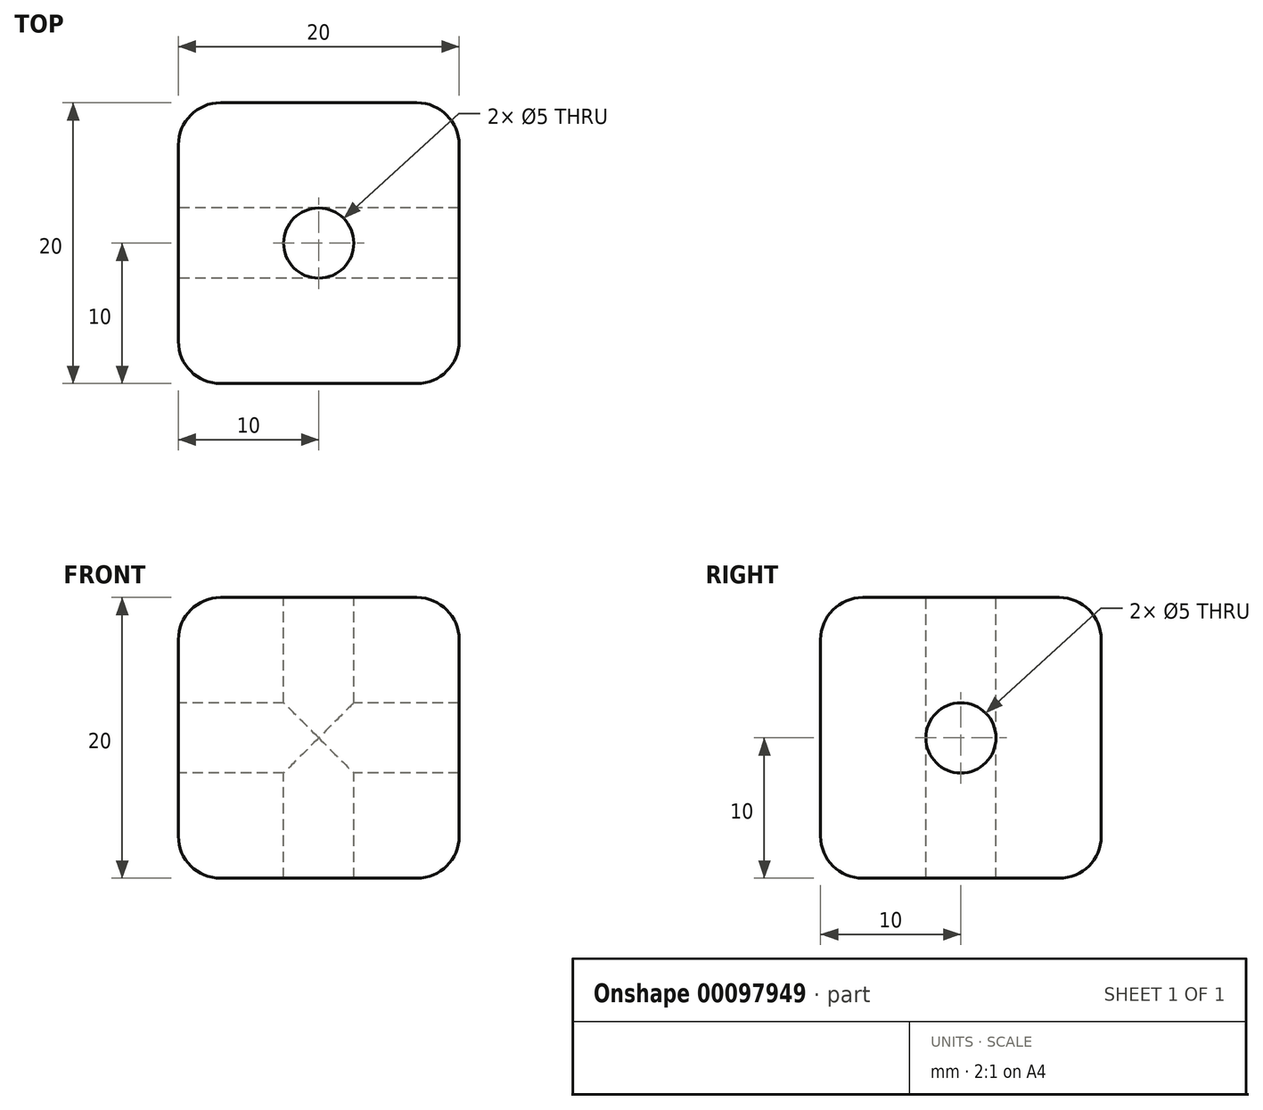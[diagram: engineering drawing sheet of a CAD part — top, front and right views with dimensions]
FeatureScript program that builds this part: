
annotation { "Feature Type Name" : "Feature", "Feature Type Description" : "" }
export const myFeature = defineFeature(function(context is Context, id is Id, definition is map)
    precondition{}
    {
        {
            var Q0;
            Q0=qCreatedBy(makeId("Top.planeOp"),FACE);
            var sketch = newSketch(context, id + "F0", { "sketchPlane" : qUnion([Q0])});
            skLineSegment(sketch, "E0.bottom", {"start": v(0, 0) * mm, "end": v(20, 0) * mm});
            skLineSegment(sketch, "E0.top", {"start": v(0, -20) * mm, "end": v(20, -20) * mm});
            skLineSegment(sketch, "E0.left", {"start": v(0, 0) * mm, "end": v(0, -20) * mm});
            skLineSegment(sketch, "E0.right", {"start": v(20, 0) * mm, "end": v(20, -20) * mm});
            skSolve(sketch);
        }
        {
            var Q0;
            Q0=makeQuery(id+"F0.imprint","IMPRINT",FACE,{"disambiguationData":[TD([[makeQuery(id+"F0.imprint","IMPRINT",EDGE,{"derivedFrom":sQuery(id+"F0.wireOp",EDGE,"E0.bottom")}),-1.0]])]});
            extrude(context, id + "F1", {"entities" : qUnion([Q0]), "depth" : 20 * mm});
        }
        {
            var Q0;
            Q0=makeQuery(id+"F1.opExtrude","CAP_FACE",FACE,{"disambiguationData":[OSD([sQuery(id+"F0.wireOp",EDGE,"E0.bottom"),sQuery(id+"F0.wireOp",EDGE,"E0.top"),sQuery(id+"F0.wireOp",EDGE,"E0.left"),sQuery(id+"F0.wireOp",EDGE,"E0.right")])],"isStart":false});
            var sketch = newSketch(context, id + "F2", { "sketchPlane" : qUnion([Q0])});
            skLineSegment(sketch, "E1", {"start": v(10, 0) * mm, "end": v(10, -20) * mm});
            skLineSegment(sketch, "E2", {"start": v(10, -20) * mm, "end": v(10, -10) * mm});
            skSolve(sketch);
        }
        {
            var Q0;
            Q0=sQuery(id+"F2.wireOp",VERTEX,"E2.end");
            var Q1;
            Q1=makeQuery(id+"F1.opExtrude","SWEPT_BODY",BODY,{"disambiguationData":[OSD([sQuery(id+"F0.wireOp",EDGE,"E0.bottom"),sQuery(id+"F0.wireOp",EDGE,"E0.top"),sQuery(id+"F0.wireOp",EDGE,"E0.left"),sQuery(id+"F0.wireOp",EDGE,"E0.right")])]});
            hole(context, id + "F3", {"style" : HoleStyle.SIMPLE, "endStyle" : HoleEndStyle.THROUGH, "holeDiameter" : 5 * mm, "locations" : qUnion([Q0]), "scope" : qUnion([Q1]), "isTappedThrough" : true});
        }
        {
            var Q0;
            Q0=makeQuery(id+"F1.opExtrude","CAP_EDGE",EDGE,{"disambiguationData":[OSD([sQuery(id+"F0.wireOp",EDGE,"E0.top")])],"isStart":false});
            var Q1;
            Q1=makeQuery(id+"F1.opExtrude","CAP_EDGE",EDGE,{"disambiguationData":[OSD([sQuery(id+"F0.wireOp",EDGE,"E0.left")])],"isStart":false});
            var Q2;
            Q2=makeQuery(id+"F1.opExtrude","CAP_EDGE",EDGE,{"disambiguationData":[OSD([sQuery(id+"F0.wireOp",EDGE,"E0.right")])],"isStart":false});
            var Q3;
            Q3=makeQuery(id+"F1.opExtrude","CAP_EDGE",EDGE,{"disambiguationData":[OSD([sQuery(id+"F0.wireOp",EDGE,"E0.bottom")])],"isStart":false});
            var Q4;
            Q4=makeQuery(id+"F1.opExtrude","SWEPT_EDGE",EDGE,{"disambiguationData":[OSD([sQuery(id+"F0.wireOp",EDGE,"E0.top"),sQuery(id+"F0.wireOp",EDGE,"E0.left")])]});
            var Q5;
            Q5=makeQuery(id+"F1.opExtrude","SWEPT_EDGE",EDGE,{"disambiguationData":[OSD([sQuery(id+"F0.wireOp",EDGE,"E0.top"),sQuery(id+"F0.wireOp",EDGE,"E0.right")])]});
            var Q6;
            Q6=makeQuery(id+"F1.opExtrude","SWEPT_EDGE",EDGE,{"disambiguationData":[OSD([sQuery(id+"F0.wireOp",EDGE,"E0.bottom"),sQuery(id+"F0.wireOp",EDGE,"E0.right")])]});
            var Q7;
            Q7=makeQuery(id+"F1.opExtrude","SWEPT_EDGE",EDGE,{"disambiguationData":[OSD([sQuery(id+"F0.wireOp",EDGE,"E0.bottom"),sQuery(id+"F0.wireOp",EDGE,"E0.left")])]});
            var Q8;
            Q8=makeQuery(id+"F1.opExtrude","CAP_EDGE",EDGE,{"disambiguationData":[OSD([sQuery(id+"F0.wireOp",EDGE,"E0.bottom")])],"isStart":true});
            var Q9;
            Q9=makeQuery(id+"F1.opExtrude","CAP_EDGE",EDGE,{"disambiguationData":[OSD([sQuery(id+"F0.wireOp",EDGE,"E0.left")])],"isStart":true});
            var Q10;
            Q10=makeQuery(id+"F1.opExtrude","CAP_EDGE",EDGE,{"disambiguationData":[OSD([sQuery(id+"F0.wireOp",EDGE,"E0.top")])],"isStart":true});
            var Q11;
            Q11=makeQuery(id+"F1.opExtrude","CAP_EDGE",EDGE,{"disambiguationData":[OSD([sQuery(id+"F0.wireOp",EDGE,"E0.right")])],"isStart":true});
            fillet(context, id + "F4", {"entities" : qUnion([Q0, Q1, Q2, Q3, Q4, Q5, Q6, Q7, Q8, Q9, Q10, Q11]), "radius" : 3 * mm, "tangentPropagation" : true, "allowEdgeOverflow" : false});
        }
        {
            var Q0;
            Q0=makeQuery(id+"F1.opExtrude","SWEPT_FACE",FACE,{"disambiguationData":[OSD([sQuery(id+"F0.wireOp",EDGE,"E0.left")])]});
            var sketch = newSketch(context, id + "F5", { "sketchPlane" : qUnion([Q0])});
            skLineSegment(sketch, "E3", {"start": v(10, 17) * mm, "end": v(10, 3) * mm});
            skLineSegment(sketch, "E4", {"start": v(10, 3) * mm, "end": v(10, 10) * mm});
            skSolve(sketch);
        }
        {
            var Q0;
            Q0=sQuery(id+"F5.wireOp",VERTEX,"E4.end");
            var Q1;
            Q1=makeQuery(id+"F1.opExtrude","SWEPT_BODY",BODY,{"disambiguationData":[OSD([sQuery(id+"F0.wireOp",EDGE,"E0.bottom"),sQuery(id+"F0.wireOp",EDGE,"E0.top"),sQuery(id+"F0.wireOp",EDGE,"E0.left"),sQuery(id+"F0.wireOp",EDGE,"E0.right")])]});
            hole(context, id + "F6", {"style" : HoleStyle.SIMPLE, "endStyle" : HoleEndStyle.THROUGH, "holeDiameter" : 5 * mm, "locations" : qUnion([Q0]), "scope" : qUnion([Q1]), "isTappedThrough" : true});
        }
    });
